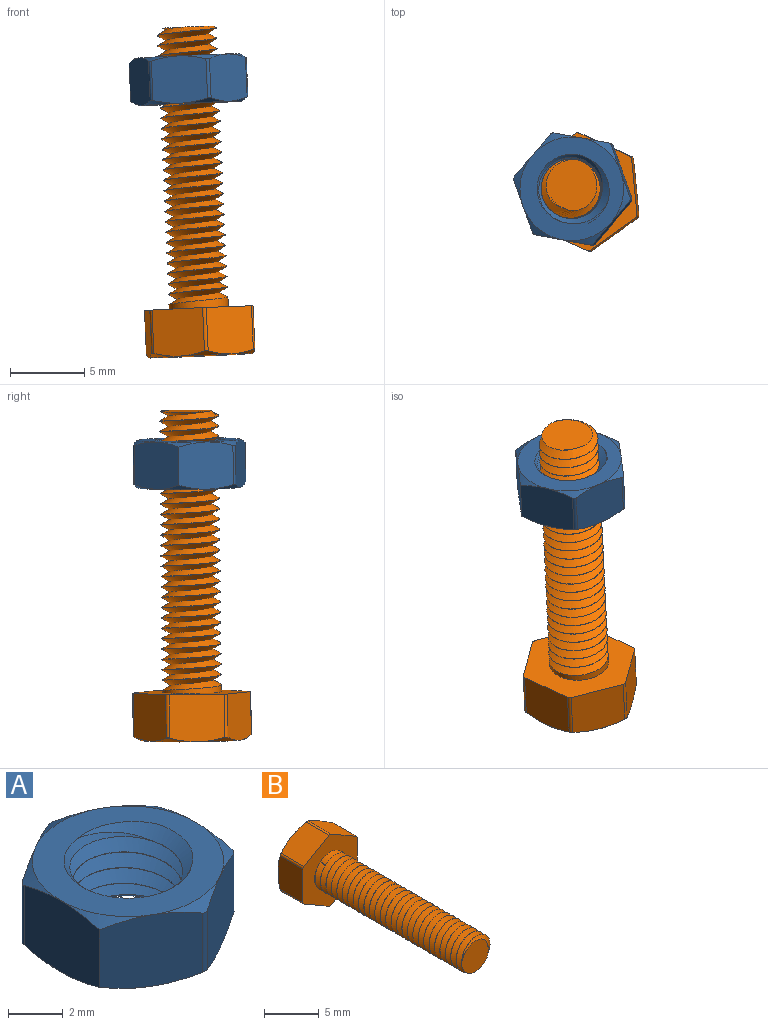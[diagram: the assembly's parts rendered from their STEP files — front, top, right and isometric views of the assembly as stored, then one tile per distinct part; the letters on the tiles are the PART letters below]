
ASSEMBLY  parts=2 mates=1
PART A: 30 faces, bbox 8.3x8.3x4.4 mm
  f0: plane 7.1x7.1mm, normal (0,0,1), area 20.5mm2, adj f5,f6,f8,f10,f12,f14,f21,f23
  f1: plane 7.12x7.12mm, normal (0,0,-1), area 20.5mm2, adj f3,f4,f7,f9,f11,f13,f22,f23
  f2: cylinder r=2mm len=4mm, axis (0,0,-1), area 1mm2, adj f21,f22,f23,f24
  f3: cone r=5.79mm half-angle=60deg, axis (0,0,1), area 1.2mm2, adj f1,f15,f16
  f4: cone r=5.79mm half-angle=60deg, axis (0,0,1), area 0.8mm2, adj f1,f15,f20,f29
  f5: cone r=5.79mm half-angle=60deg, axis (0,0,-1), area 1.2mm2, adj f0,f15,f16
  f6: cone r=5.79mm half-angle=60deg, axis (0,0,-1), area 0.8mm2, adj f0,f15,f20,f29
  f7: cone r=5.79mm half-angle=60deg, axis (0,0,1), area 0.8mm2, adj f1,f16,f17,f28
  f8: cone r=5.79mm half-angle=60deg, axis (0,0,-1), area 0.8mm2, adj f0,f16,f17,f28
  f9: cone r=5.79mm half-angle=60deg, axis (0,0,1), area 0.8mm2, adj f1,f17,f18,f27
  f10: cone r=5.79mm half-angle=60deg, axis (0,0,-1), area 0.8mm2, adj f0,f17,f18,f27
  f11: cone r=5.79mm half-angle=60deg, axis (0,0,1), area 0.8mm2, adj f1,f18,f19,f26
  f12: cone r=5.79mm half-angle=60deg, axis (0,0,-1), area 0.8mm2, adj f0,f18,f19,f26
  f13: cone r=5.79mm half-angle=60deg, axis (0,0,1), area 0.8mm2, adj f1,f19,f20,f25
  f14: cone r=5.79mm half-angle=60deg, axis (0,0,-1), area 0.8mm2, adj f0,f19,f20,f25
  f15: plane 3.71x3.54mm, normal (-0.5,-0.87,0), area 11.7mm2, adj f3,f4,f5,f6,f16,f29
  f16: plane 4.23x3.53mm, normal (-1,0,0), area 11.7mm2, adj f3,f5,f7,f8,f15,f28
  f17: plane 3.26x3.21mm, normal (-0.5,0.87,0), area 11.3mm2, adj f7,f8,f9,f10,f27,f28
  f18: plane 3.26x3.21mm, normal (0.5,0.87,0), area 11.3mm2, adj f9,f10,f11,f12,f26,f27
  f19: plane 3.76x3.2mm, normal (1,0,0), area 11.3mm2, adj f11,f12,f13,f14,f25,f26
  f20: plane 3.26x3.21mm, normal (0.5,-0.87,0), area 11.3mm2, adj f4,f6,f13,f14,f25,f29
  f21: cone r=2mm half-angle=45deg, axis (0,0,1), area 2mm2, adj f0,f2,f23,f24
  f22: cone r=2.34mm half-angle=45deg, axis (0,0,-1), area 2mm2, adj f1,f2,f23,f24
  f23: bspline ~5.99x5.19mm, area 42.8mm2, adj f0,f1,f2,f21,f22,f24
  f24: bspline ~5.99x5.19mm, area 42.8mm2, adj f0,f1,f2,f21,f22,f23
  f25: cylinder r=0.25mm len=2.66mm, axis (0,0,-1), area 0.7mm2, adj f13,f14,f19,f20
  f26: cylinder r=0.25mm len=2.66mm, axis (0,0,-1), area 0.7mm2, adj f11,f12,f18,f19
  f27: cylinder r=0.25mm len=2.66mm, axis (0,0,-1), area 0.7mm2, adj f9,f10,f17,f18
  f28: cylinder r=0.25mm len=2.66mm, axis (0,0,-1), area 0.7mm2, adj f7,f8,f16,f17
  f29: cylinder r=0.25mm len=2.66mm, axis (0,0,-1), area 0.7mm2, adj f4,f6,f15,f20
PART B: 25 faces, bbox 8.4x23.1x8.5 mm
  f0: cylinder r=2mm len=19mm, axis (0,1,0), area -72.6mm2, adj f7,f15,f16,f17,f18
  f1: plane 3.26x3.2mm, normal (0.5,0,-0.87), area 11.7mm2, adj f7,f9,f13,f19,f24
  f2: plane 3.76x3.2mm, normal (1,0,0), area 11.7mm2, adj f7,f12,f13,f19,f20
  f3: plane 3.26x3.2mm, normal (0.5,0,0.87), area 11.7mm2, adj f7,f11,f12,f20,f21
  f4: plane 3.26x3.2mm, normal (-0.5,0,0.87), area 11.7mm2, adj f7,f10,f11,f21,f22
  f5: plane 3.76x3.2mm, normal (-1,0,0), area 11.7mm2, adj f7,f8,f10,f22,f23
  f6: plane 3.26x3.2mm, normal (-0.5,0,-0.87), area 11.7mm2, adj f7,f8,f9,f23,f24
  f7: plane 8.01x7mm, normal (0,-1,0), area 29.8mm2, adj f0,f1,f2,f3,f4,f5,f6,f17
  f8: cone r=5.79mm half-angle=60deg, axis (0,-1,0), area 0.8mm2, adj f5,f6,f14,f23
  f9: cone r=5.79mm half-angle=60deg, axis (0,-1,0), area 0.8mm2, adj f1,f6,f14,f24
  f10: cone r=5.79mm half-angle=60deg, axis (0,-1,0), area 0.8mm2, adj f4,f5,f14,f22
  f11: cone r=5.79mm half-angle=60deg, axis (0,-1,0), area 0.8mm2, adj f3,f4,f14,f21
  f12: cone r=5.79mm half-angle=60deg, axis (0,-1,0), area 0.8mm2, adj f2,f3,f14,f20
  f13: cone r=5.79mm half-angle=60deg, axis (0,-1,0), area 0.8mm2, adj f1,f2,f14,f19
  f14: plane 7x7mm, normal (0,1,0), area 38.5mm2, adj f8,f9,f10,f11,f12,f13
  f15: plane 3.92x3.91mm, normal (0,-1,0), area 9.3mm2, adj f0,f17,f18
  f16: plane 0.69x0.47mm, normal (-0.78,0,-0.62), area 0.2mm2, adj f0,f17,f18
  f17: bspline ~19.36x4.62mm, area 196.1mm2, adj f0,f7,f15,f16,f18
  f18: bspline ~19.13x4.62mm, area 193.2mm2, adj f0,f15,f16,f17
  f19: cylinder r=0.25mm len=2.93mm, axis (0,1,0), area 0.8mm2, adj f1,f2,f7,f13
  f20: cylinder r=0.25mm len=2.93mm, axis (0,1,0), area 0.8mm2, adj f2,f3,f7,f12
  f21: cylinder r=0.25mm len=2.93mm, axis (0,1,0), area 0.8mm2, adj f3,f4,f7,f11
  f22: cylinder r=0.25mm len=2.93mm, axis (0,1,0), area 0.8mm2, adj f4,f5,f7,f10
  f23: cylinder r=0.25mm len=2.93mm, axis (0,1,0), area 0.8mm2, adj f5,f6,f7,f8
  f24: cylinder r=0.25mm len=2.93mm, axis (0,1,0), area 0.8mm2, adj f1,f6,f7,f9
PLACE A rot(axis=(0.01,-0.06,-1),40.4deg) t=(5.2,11.15,21.73)mm
PLACE B rot(axis=(-0.4,0.63,-0.66),133.6deg) t=(5.94,10.98,4.69)mm
MATE cylindrical B.f0 <-> A.f3  axis (-0.04,0.01,1) through (4.98,11.2,26.87)mm
